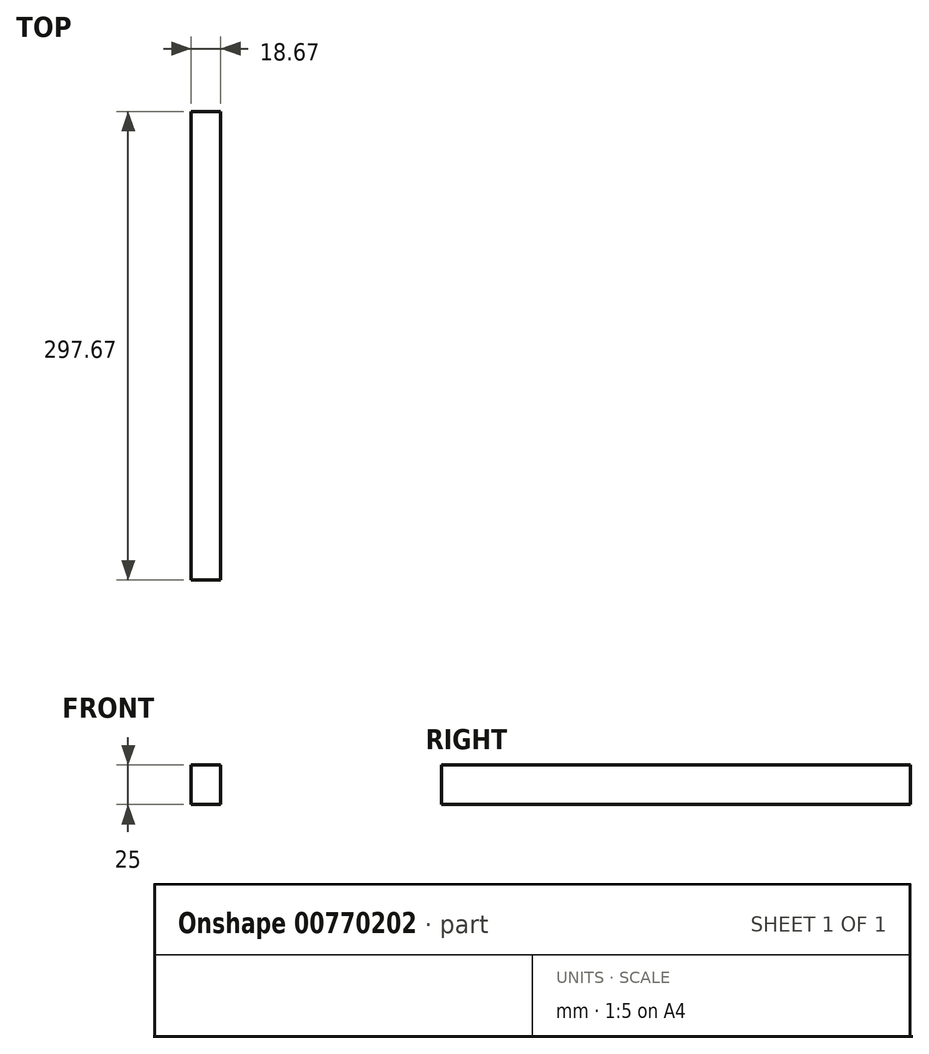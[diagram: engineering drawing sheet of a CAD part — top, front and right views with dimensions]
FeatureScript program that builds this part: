
annotation { "Feature Type Name" : "Feature", "Feature Type Description" : "" }
export const myFeature = defineFeature(function(context is Context, id is Id, definition is map)
    precondition{}
    {
        {
            var Q0;
            Q0=qCreatedBy(makeId("Top.planeOp"),FACE);
            var sketch = newSketch(context, id + "F0", { "sketchPlane" : qUnion([Q0])});
            skLineSegment(sketch, "E0.bottom", {"start": v(-203.68, 110.14) * mm, "end": v(-185.01, 110.14) * mm});
            skLineSegment(sketch, "E0.top", {"start": v(-203.68, -187.53) * mm, "end": v(-185.01, -187.53) * mm});
            skLineSegment(sketch, "E0.left", {"start": v(-203.68, 110.14) * mm, "end": v(-203.68, -187.53) * mm});
            skLineSegment(sketch, "E0.right", {"start": v(-185.01, 110.14) * mm, "end": v(-185.01, -187.53) * mm});
            skPoint(sketch, "E0.middle", {"position": v(-194.35, -38.7) * mm});
            skSolve(sketch);
        }
        {
            var Q0;
            Q0 = qSketchRegion(id + "F0", true);
            extrude(context, id + "F1", {"entities" : qUnion([Q0]), "depth" : 25 * mm, "offsetDistance" : 25 * mm});
        }
    });
